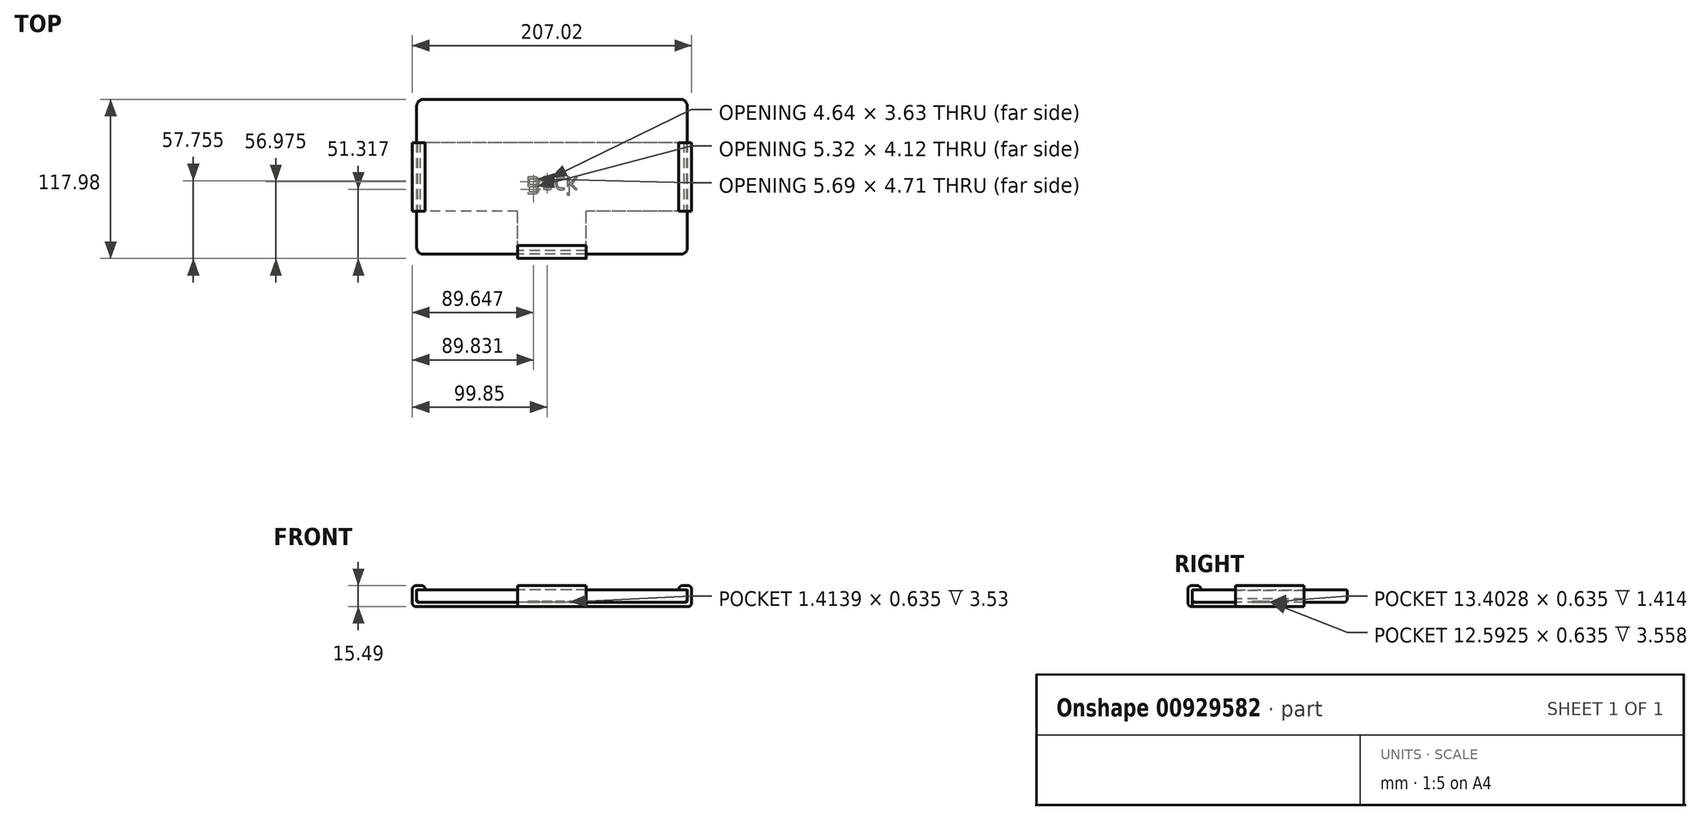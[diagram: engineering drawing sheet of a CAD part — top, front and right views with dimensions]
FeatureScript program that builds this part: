
annotation { "Feature Type Name" : "Feature", "Feature Type Description" : "" }
export const myFeature = defineFeature(function(context is Context, id is Id, definition is map)
    precondition{}
    {
        {
            var Q0;
            Q0=qCreatedBy(makeId("Top.planeOp"),FACE);
            var sketch = newSketch(context, id + "F0", { "sketchPlane" : qUnion([Q0])});
            skLineSegment(sketch, "E0.bottom", {"start": v(100.33, 57.4) * mm, "end": v(-100.33, 57.4) * mm});
            skLineSegment(sketch, "E0.top", {"start": v(100.33, -57.4) * mm, "end": v(-100.33, -57.4) * mm});
            skLineSegment(sketch, "E0.left", {"start": v(100.33, 57.4) * mm, "end": v(100.33, -57.4) * mm});
            skLineSegment(sketch, "E0.right", {"start": v(-100.33, 57.4) * mm, "end": v(-100.33, -57.4) * mm});
            skPoint(sketch, "E0.middle", {"position": v(0, 0) * mm});
            skSolve(sketch);
        }
        {
            var Q0;
            Q0=makeQuery(id+"F0.imprint","IMPRINT",FACE,{"disambiguationData":[TD([[makeQuery(id+"F0.imprint","IMPRINT",EDGE,{"derivedFrom":sQuery(id+"F0.wireOp",EDGE,"E0.bottom")}),1.0]])]});
            extrude(context, id + "F1", {"entities" : qUnion([Q0]), "depth" : 9.14 * mm, "offsetDistance" : 25.4 * mm});
        }
        {
            var Q0;
            Q0=makeQuery(id+"F1.opExtrude","SWEPT_EDGE",EDGE,{"disambiguationData":[OSD([sQuery(id+"F0.wireOp",EDGE,"E0.top"),sQuery(id+"F0.wireOp",EDGE,"E0.right")])]});
            var Q1;
            Q1=makeQuery(id+"F1.opExtrude","SWEPT_EDGE",EDGE,{"disambiguationData":[OSD([sQuery(id+"F0.wireOp",EDGE,"E0.top"),sQuery(id+"F0.wireOp",EDGE,"E0.left")])]});
            var Q2;
            Q2=makeQuery(id+"F1.opExtrude","SWEPT_EDGE",EDGE,{"disambiguationData":[OSD([sQuery(id+"F0.wireOp",EDGE,"E0.bottom"),sQuery(id+"F0.wireOp",EDGE,"E0.left")])]});
            var Q3;
            Q3=makeQuery(id+"F1.opExtrude","SWEPT_EDGE",EDGE,{"disambiguationData":[OSD([sQuery(id+"F0.wireOp",EDGE,"E0.bottom"),sQuery(id+"F0.wireOp",EDGE,"E0.right")])]});
            fillet(context, id + "F2", {"entities" : qUnion([Q0, Q1, Q2, Q3]), "radius" : 5.08 * mm, "tangentPropagation" : true, "allowEdgeOverflow" : false});
        }
        {
            var Q0;
            Q0=makeQuery(id+"F1.opExtrude","CAP_FACE",FACE,{"disambiguationData":[OSD([sQuery(id+"F0.wireOp",EDGE,"E0.bottom"),sQuery(id+"F0.wireOp",EDGE,"E0.top"),sQuery(id+"F0.wireOp",EDGE,"E0.left"),sQuery(id+"F0.wireOp",EDGE,"E0.right")])],"isStart":true});
            fillet(context, id + "F3", {"entities" : qUnion([Q0]), "radius" : 2.54 * mm, "tangentPropagation" : true, "allowEdgeOverflow" : false});
        }
        {
            var Q0;
            Q0=makeQuery(id+"F1.opExtrude","CAP_FACE",FACE,{"disambiguationData":[OSD([sQuery(id+"F0.wireOp",EDGE,"E0.bottom"),sQuery(id+"F0.wireOp",EDGE,"E0.top"),sQuery(id+"F0.wireOp",EDGE,"E0.left"),sQuery(id+"F0.wireOp",EDGE,"E0.right")])],"isStart":false});
            fillet(context, id + "F4", {"entities" : qUnion([Q0]), "radius" : 0.64 * mm, "tangentPropagation" : true, "allowEdgeOverflow" : false});
        }
        {
            var Q0;
            Q0=makeQuery(id+"F1.opExtrude","CAP_FACE",FACE,{"disambiguationData":[OSD([sQuery(id+"F0.wireOp",EDGE,"E0.bottom"),sQuery(id+"F0.wireOp",EDGE,"E0.top"),sQuery(id+"F0.wireOp",EDGE,"E0.left"),sQuery(id+"F0.wireOp",EDGE,"E0.right")])],"isStart":false});
            var sketch = newSketch(context, id + "F5", { "sketchPlane" : qUnion([Q0])});
            skText(sketch, "E1", { "text": "Front", "fontName": "OpenSans-Regular.ttf"});
            const initialGuessF5  = {"E1": [-0.02225, 0, 1, 0, 0.0127]};
            skSetInitialGuess(sketch, initialGuessF5);
            skSolve(sketch);
        }
        {
            var Q0;
            Q0=makeQuery(id+"F1.opExtrude","CAP_FACE",FACE,{"disambiguationData":[OSD([sQuery(id+"F0.wireOp",EDGE,"E0.bottom"),sQuery(id+"F0.wireOp",EDGE,"E0.top"),sQuery(id+"F0.wireOp",EDGE,"E0.left"),sQuery(id+"F0.wireOp",EDGE,"E0.right")])],"isStart":true});
            var sketch = newSketch(context, id + "F6", { "sketchPlane" : qUnion([Q0])});
            skText(sketch, "E2", { "text": "Back", "fontName": "OpenSans-Regular.ttf"});
            const initialGuessF6  = {"E2": [-0.01972, 0, 1, 0, 0.0127]};
            skSetInitialGuess(sketch, initialGuessF6);
            skSolve(sketch);
        }
        {
            var Q0;
            Q0=qSketchRegion(id+"F6",true);
            var Q1;
            Q1=qConstructionFilter(qBodyType(qCreatedBy(id+"F6",EDGE),BodyType.WIRE),ConstructionObject.NO);
            extrude(context, id + "F7", {"entities" : qUnion([Q0]), "operationType" : NewBodyOperationType.REMOVE, "surfaceEntities" : qUnion([Q1]), "oppositeDirection" : true, "depth" : 0.64 * mm, "offsetDistance" : 25.4 * mm});
        }
        {
            var Q0;
            Q0=qCreatedBy(makeId("Front.planeOp"),FACE);
            var sketch = newSketch(context, id + "F8", { "sketchPlane" : qUnion([Q0])});
            skPoint(sketch, "E3.0", {"position": v(100.33, 5.52) * mm});
            skPoint(sketch, "E4.0", {"position": v(95.25, 9.14) * mm});
            skPoint(sketch, "E5.0", {"position": v(-100.33, 2.54) * mm});
            skPoint(sketch, "E6.0", {"position": v(-95.25, 0) * mm});
            skLineSegment(sketch, "E7.top", {"start": v(100.33, 0) * mm, "end": v(-100.33, 0) * mm});
            skLineSegment(sketch, "E7.left", {"start": v(100.33, 9.14) * mm, "end": v(100.33, 0) * mm});
            skLineSegment(sketch, "E7.right", {"start": v(-100.33, 9.14) * mm, "end": v(-100.33, 0) * mm});
            skLineSegment(sketch, "E8", {"start": v(-100.33, 9.14) * mm, "end": v(-93.98, 9.14) * mm});
            skLineSegment(sketch, "E9", {"start": v(-93.98, 9.14) * mm, "end": v(-93.98, 12.32) * mm});
            skLineSegment(sketch, "E10", {"start": v(-93.98, 12.32) * mm, "end": v(-103.5, 12.32) * mm});
            skLineSegment(sketch, "E11", {"start": v(-103.5, 12.32) * mm, "end": v(-103.5, -3.18) * mm});
            skLineSegment(sketch, "E12", {"start": v(100.33, 9.14) * mm, "end": v(93.98, 9.14) * mm});
            skLineSegment(sketch, "E13", {"start": v(93.98, 9.14) * mm, "end": v(93.98, 12.32) * mm});
            skLineSegment(sketch, "E14", {"start": v(93.98, 12.32) * mm, "end": v(103.5, 12.32) * mm});
            skLineSegment(sketch, "E15", {"start": v(103.5, 12.32) * mm, "end": v(103.5, -3.17) * mm});
            skLineSegment(sketch, "E16", {"start": v(103.5, -3.17) * mm, "end": v(-103.5, -3.18) * mm});
            skSolve(sketch);
        }
        {
            var Q0;
            Q0=makeQuery(id+"F8.imprint","IMPRINT",FACE,{"disambiguationData":[TD([[makeQuery(id+"F8.imprint","IMPRINT",EDGE,{"derivedFrom":sQuery(id+"F8.wireOp",EDGE,"E7.top")}),1.0]])]});
            extrude(context, id + "F9", {"entities" : qUnion([Q0]), "endBound" : BoundingType.SYMMETRIC, "depth" : 50.8 * mm, "offsetDistance" : 25.4 * mm});
        }
        {
            var Q0;
            Q0=makeQuery(id+"F9.opExtrude","SWEPT_EDGE",EDGE,{"disambiguationData":[OSD([sQuery(id+"F8.wireOp",EDGE,"E14"),sQuery(id+"F8.wireOp",EDGE,"E15")])]});
            var Q1;
            Q1=makeQuery(id+"F9.opExtrude","SWEPT_EDGE",EDGE,{"disambiguationData":[OSD([sQuery(id+"F8.wireOp",EDGE,"E15"),sQuery(id+"F8.wireOp",EDGE,"E16")])]});
            var Q2;
            Q2=makeQuery(id+"F9.opExtrude","SWEPT_EDGE",EDGE,{"disambiguationData":[OSD([sQuery(id+"F8.wireOp",EDGE,"E10"),sQuery(id+"F8.wireOp",EDGE,"E11")])]});
            var Q3;
            Q3=makeQuery(id+"F9.opExtrude","SWEPT_EDGE",EDGE,{"disambiguationData":[OSD([sQuery(id+"F8.wireOp",EDGE,"E11"),sQuery(id+"F8.wireOp",EDGE,"E16")])]});
            var Q4;
            Q4=makeQuery(id+"F9.opExtrude","SWEPT_EDGE",EDGE,{"disambiguationData":[OSD([sQuery(id+"F8.wireOp",EDGE,"E9"),sQuery(id+"F8.wireOp",EDGE,"E10")])]});
            var Q5;
            Q5=makeQuery(id+"F9.opExtrude","SWEPT_EDGE",EDGE,{"disambiguationData":[OSD([sQuery(id+"F8.wireOp",EDGE,"E13"),sQuery(id+"F8.wireOp",EDGE,"E14")])]});
            fillet(context, id + "F10", {"entities" : qUnion([Q0, Q1, Q2, Q3, Q4, Q5]), "radius" : 2.54 * mm, "tangentPropagation" : true, "allowEdgeOverflow" : false});
        }
        {
            var Q0;
            Q0=makeQuery(id+"F9.opExtrude","SWEPT_EDGE",EDGE,{"disambiguationData":[OSD([sQuery(id+"F8.wireOp",EDGE,"E7.top"),sQuery(id+"F8.wireOp",EDGE,"E7.left")])]});
            var Q1;
            Q1=makeQuery(id+"F9.opExtrude","SWEPT_EDGE",EDGE,{"disambiguationData":[OSD([sQuery(id+"F8.wireOp",EDGE,"E7.top"),sQuery(id+"F8.wireOp",EDGE,"E7.right")])]});
            fillet(context, id + "F11", {"entities" : qUnion([Q0, Q1]), "radius" : 1.27 * mm, "tangentPropagation" : true, "allowEdgeOverflow" : false});
        }
        {
            var Q0;
            Q0=makeQuery(id+"F9.opExtrude","CAP_FACE",FACE,{"disambiguationData":[OSD([sQuery(id+"F8.wireOp",EDGE,"E7.top"),sQuery(id+"F8.wireOp",EDGE,"E7.left"),sQuery(id+"F8.wireOp",EDGE,"E7.right"),sQuery(id+"F8.wireOp",EDGE,"E8"),sQuery(id+"F8.wireOp",EDGE,"E9"),sQuery(id+"F8.wireOp",EDGE,"E10"),sQuery(id+"F8.wireOp",EDGE,"E11"),sQuery(id+"F8.wireOp",EDGE,"E12"),sQuery(id+"F8.wireOp",EDGE,"E13"),sQuery(id+"F8.wireOp",EDGE,"E14"),sQuery(id+"F8.wireOp",EDGE,"E15"),sQuery(id+"F8.wireOp",EDGE,"E16")])],"isStart":false});
            var sketch = newSketch(context, id + "F12", { "sketchPlane" : qUnion([Q0])});
            skPoint(sketch, "E17.0", {"position": v(0, 0) * mm});
            skLineSegment(sketch, "E18.bottom", {"start": v(0, 0) * mm, "end": v(25.4, 0) * mm});
            skLineSegment(sketch, "E18.top", {"start": v(0, -3.17) * mm, "end": v(25.4, -3.17) * mm});
            skLineSegment(sketch, "E18.right", {"start": v(25.4, 0) * mm, "end": v(25.4, -3.17) * mm});
            skLineSegment(sketch, "E19.bottom", {"start": v(0, 0) * mm, "end": v(-25.4, 0) * mm});
            skLineSegment(sketch, "E19.top", {"start": v(0, -3.17) * mm, "end": v(-25.4, -3.17) * mm});
            skLineSegment(sketch, "E19.right", {"start": v(-25.4, 0) * mm, "end": v(-25.4, -3.17) * mm});
            skSolve(sketch);
        }
        {
            var Q0;
            Q0=makeQuery(id+"F12.imprint","IMPRINT",FACE,{"disambiguationData":[TD([[makeQuery(id+"F12.imprint","IMPRINT",EDGE,{"derivedFrom":sQuery(id+"F12.wireOp",EDGE,"E18.bottom")}),1.0]])]});
            extrude(context, id + "F13", {"entities" : qUnion([Q0]), "operationType" : NewBodyOperationType.ADD, "depth" : 32 * mm, "offsetDistance" : 25.4 * mm});
        }
        {
            var Q0;
            Q0=qCreatedBy(makeId("Right.planeOp"),FACE);
            var sketch = newSketch(context, id + "F14", { "sketchPlane" : qUnion([Q0])});
            skPoint(sketch, "E20.0", {"position": v(-57.4, 0) * mm});
            skPoint(sketch, "E21.0", {"position": v(-52.32, 9.14) * mm});
            skLineSegment(sketch, "E22", {"start": v(-57.4, 0) * mm, "end": v(-57.4, 9.14) * mm});
            skLineSegment(sketch, "E23", {"start": v(-57.4, 9.14) * mm, "end": v(-51.05, 9.14) * mm});
            skLineSegment(sketch, "E24", {"start": v(-51.05, 9.14) * mm, "end": v(-51.05, 12.32) * mm});
            skLineSegment(sketch, "E25", {"start": v(-51.05, 12.32) * mm, "end": v(-60.58, 12.32) * mm});
            skLineSegment(sketch, "E26", {"start": v(-60.58, 12.32) * mm, "end": v(-60.58, -3.18) * mm});
            skLineSegment(sketch, "E27", {"start": v(-60.58, -3.18) * mm, "end": v(-57.4, -3.18) * mm});
            skLineSegment(sketch, "E28", {"start": v(-57.4, -3.18) * mm, "end": v(-57.4, 0) * mm});
            skSolve(sketch);
        }
        {
            var Q0;
            Q0=makeQuery(id+"F14.imprint","IMPRINT",FACE,{"disambiguationData":[TD([[makeQuery(id+"F14.imprint","IMPRINT",EDGE,{"derivedFrom":sQuery(id+"F14.wireOp",EDGE,"E22")}),1.0]])]});
            extrude(context, id + "F15", {"entities" : qUnion([Q0]), "endBound" : BoundingType.SYMMETRIC, "depth" : 50.8 * mm, "offsetDistance" : 25.4 * mm});
        }
        {
            var Q0;
            Q0=makeQuery(id+"F15.opExtrude","SWEPT_EDGE",EDGE,{"disambiguationData":[OSD([sQuery(id+"F14.wireOp",EDGE,"E25"),sQuery(id+"F14.wireOp",EDGE,"E26")])]});
            var Q1;
            Q1=makeQuery(id+"F15.opExtrude","SWEPT_EDGE",EDGE,{"disambiguationData":[OSD([sQuery(id+"F14.wireOp",EDGE,"E24"),sQuery(id+"F14.wireOp",EDGE,"E25")])]});
            var Q2;
            Q2=makeQuery(id+"F15.opExtrude","SWEPT_EDGE",EDGE,{"disambiguationData":[OSD([sQuery(id+"F14.wireOp",EDGE,"E26"),sQuery(id+"F14.wireOp",EDGE,"E27")])]});
            fillet(context, id + "F16", {"entities" : qUnion([Q0, Q1, Q2]), "radius" : 2.54 * mm, "tangentPropagation" : true, "allowEdgeOverflow" : false});
        }
        {
            var Q0;
            Q0=makeQuery(id+"F13.opExtrude","CAP_EDGE",EDGE,{"disambiguationData":[OSD([sQuery(id+"F12.wireOp",EDGE,"E18.bottom"),sQuery(id+"F12.wireOp",EDGE,"E19.bottom")])],"isStart":false});
            fillet(context, id + "F17", {"entities" : qUnion([Q0]), "radius" : 1.27 * mm, "tangentPropagation" : true, "allowEdgeOverflow" : false});
        }
    });
